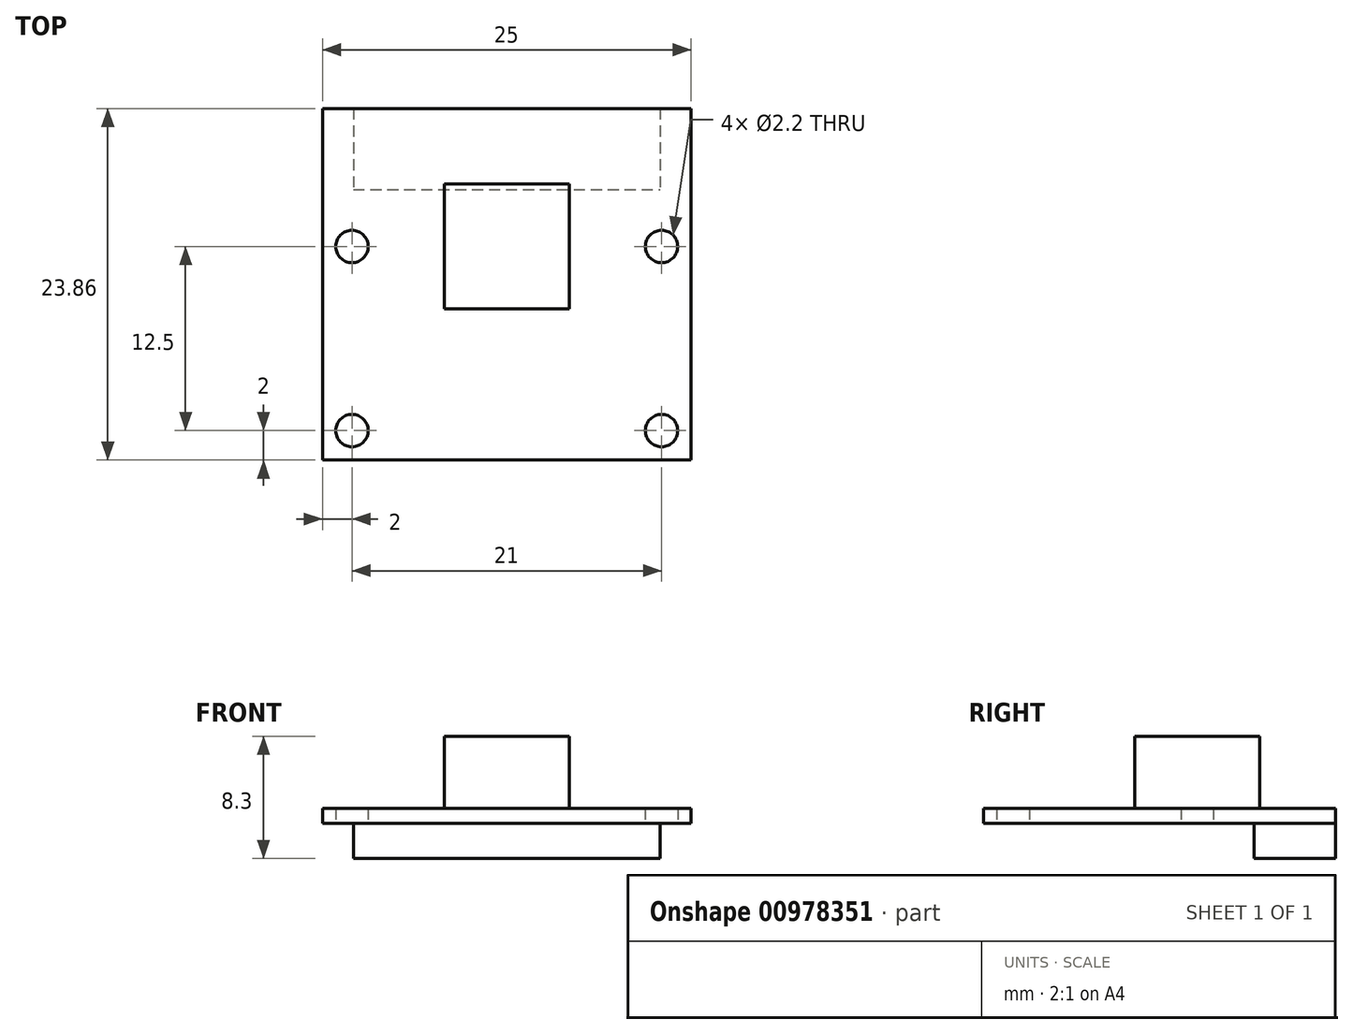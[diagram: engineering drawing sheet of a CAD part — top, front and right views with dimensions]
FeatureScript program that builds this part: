
annotation { "Feature Type Name" : "Feature", "Feature Type Description" : "" }
export const myFeature = defineFeature(function(context is Context, id is Id, definition is map)
    precondition{}
    {
        {
            var Q0;
            Q0=qCreatedBy(makeId("Top.planeOp"),FACE);
            var sketch = newSketch(context, id + "F0", { "sketchPlane" : qUnion([Q0])});
            skLineSegment(sketch, "E0.bottom", {"start": v(0, 0) * mm, "end": v(25, 0) * mm});
            skLineSegment(sketch, "E0.top", {"start": v(0, 23.86) * mm, "end": v(25, 23.86) * mm});
            skLineSegment(sketch, "E0.left", {"start": v(0, 0) * mm, "end": v(0, 23.86) * mm});
            skLineSegment(sketch, "E0.right", {"start": v(25, 0) * mm, "end": v(25, 23.86) * mm});
            skCircle(sketch, "E1", {"center": v(2, 2) * mm, "radius": 1.1 * mm});
            skCircle(sketch, "E2", {"center": v(23, 2) * mm, "radius": 1.1 * mm});
            skCircle(sketch, "E3", {"center": v(23, 14.5) * mm, "radius": 1.1 * mm});
            skCircle(sketch, "E4", {"center": v(2, 14.5) * mm, "radius": 1.1 * mm});
            skSolve(sketch);
        }
        {
            var Q0;
            Q0=makeQuery(id+"F0.imprint","IMPRINT",FACE,{"disambiguationData":[TD([[makeQuery(id+"F0.imprint","IMPRINT",EDGE,{"derivedFrom":sQuery(id+"F0.wireOp",EDGE,"E0.bottom")}),1.0]])]});
            extrude(context, id + "F1", {"entities" : qUnion([Q0]), "depth" : 1 * mm, "offsetDistance" : 25 * mm});
        }
        {
            var Q0;
            Q0=makeQuery(id+"F1.opExtrude","CAP_FACE",FACE,{"disambiguationData":[OSD([sQuery(id+"F0.wireOp",EDGE,"E0.bottom"),sQuery(id+"F0.wireOp",EDGE,"E0.top"),sQuery(id+"F0.wireOp",EDGE,"E0.left"),sQuery(id+"F0.wireOp",EDGE,"E0.right"),sQuery(id+"F0.wireOp",EDGE,"E1"),sQuery(id+"F0.wireOp",EDGE,"E2"),sQuery(id+"F0.wireOp",EDGE,"E3"),sQuery(id+"F0.wireOp",EDGE,"E4")])],"isStart":true});
            var sketch = newSketch(context, id + "F2", { "sketchPlane" : qUnion([Q0])});
            skLineSegment(sketch, "E5.0.0", {"start": v(0, -23.86) * mm, "end": v(25, -23.86) * mm});
            skLineSegment(sketch, "E5.0.1", {"start": v(25, -23.86) * mm, "end": v(25, 0) * mm});
            skLineSegment(sketch, "E5.0.2", {"start": v(25, 0) * mm, "end": v(0, 0) * mm});
            skLineSegment(sketch, "E5.0.3", {"start": v(0, 0) * mm, "end": v(0, -23.86) * mm});
            skLineSegment(sketch, "E6.bottom", {"start": v(2.1, -23.86) * mm, "end": v(22.9, -23.86) * mm});
            skLineSegment(sketch, "E6.top", {"start": v(2.1, -18.36) * mm, "end": v(22.9, -18.36) * mm});
            skLineSegment(sketch, "E6.left", {"start": v(2.1, -23.86) * mm, "end": v(2.1, -18.36) * mm});
            skLineSegment(sketch, "E6.right", {"start": v(22.9, -23.86) * mm, "end": v(22.9, -18.36) * mm});
            skPoint(sketch, "E7", {"position": v(12.5, -23.86) * mm});
            skSolve(sketch);
        }
        {
            var Q0;
            Q0=makeQuery(id+"F2.imprint","IMPRINT",FACE,{"disambiguationData":[TD([[makeQuery(id+"F2.imprint","IMPRINT",EDGE,{"derivedFrom":sQuery(id+"F2.wireOp",EDGE,"E6.top")}),-1.0]])]});
            extrude(context, id + "F3", {"entities" : qUnion([Q0]), "operationType" : NewBodyOperationType.ADD, "depth" : 2.4 * mm, "offsetDistance" : 25 * mm});
        }
        {
            var Q0;
            Q0=makeQuery(id+"F1.opExtrude","CAP_FACE",FACE,{"disambiguationData":[OSD([sQuery(id+"F0.wireOp",EDGE,"E0.bottom"),sQuery(id+"F0.wireOp",EDGE,"E0.top"),sQuery(id+"F0.wireOp",EDGE,"E0.left"),sQuery(id+"F0.wireOp",EDGE,"E0.right"),sQuery(id+"F0.wireOp",EDGE,"E1"),sQuery(id+"F0.wireOp",EDGE,"E2"),sQuery(id+"F0.wireOp",EDGE,"E3"),sQuery(id+"F0.wireOp",EDGE,"E4")])],"isStart":false});
            var sketch = newSketch(context, id + "F4", { "sketchPlane" : qUnion([Q0])});
            skLineSegment(sketch, "E8.bottom", {"start": v(16.75, 18.75) * mm, "end": v(8.25, 18.75) * mm});
            skLineSegment(sketch, "E8.top", {"start": v(16.75, 10.25) * mm, "end": v(8.25, 10.25) * mm});
            skLineSegment(sketch, "E8.left", {"start": v(16.75, 18.75) * mm, "end": v(16.75, 10.25) * mm});
            skLineSegment(sketch, "E8.right", {"start": v(8.25, 18.75) * mm, "end": v(8.25, 10.25) * mm});
            skPoint(sketch, "E8.middle", {"position": v(12.5, 14.5) * mm});
            skPoint(sketch, "E8.middle.positionSnap0", {"position": v(12.5, 0) * mm});
            skPoint(sketch, "E8.centerSnap0", {"position": v(12.5, 0) * mm});
            skSolve(sketch);
        }
        {
            var Q0;
            Q0=makeQuery(id+"F4.imprint","IMPRINT",FACE,{"disambiguationData":[TD([[makeQuery(id+"F4.imprint","IMPRINT",EDGE,{"derivedFrom":sQuery(id+"F4.wireOp",EDGE,"E8.bottom")}),1.0]])]});
            extrude(context, id + "F5", {"entities" : qUnion([Q0]), "operationType" : NewBodyOperationType.ADD, "depth" : 4.9 * mm, "offsetDistance" : 25 * mm});
        }
    });
